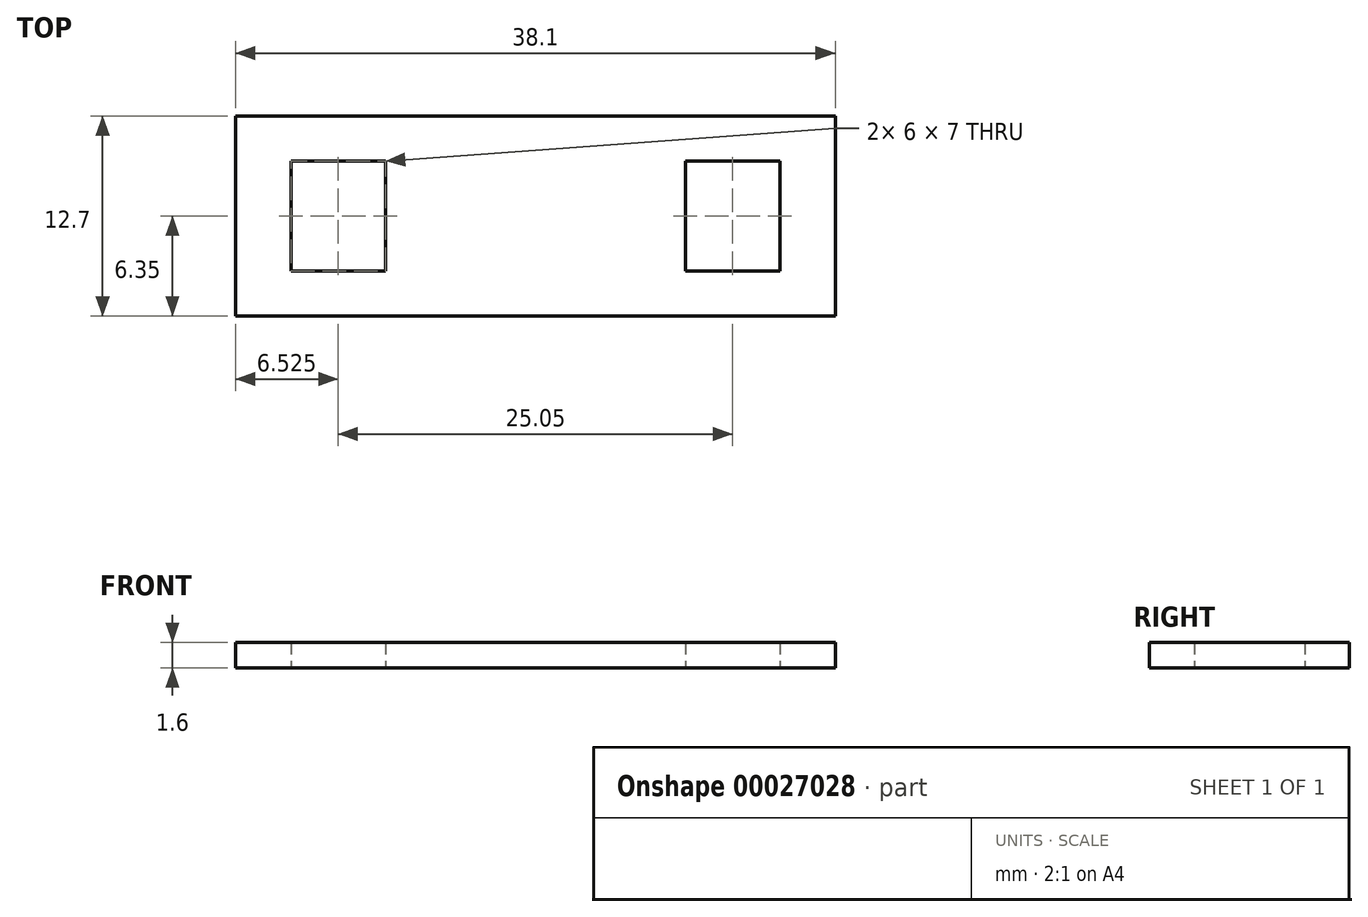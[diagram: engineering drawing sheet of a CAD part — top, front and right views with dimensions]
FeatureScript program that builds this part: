
annotation { "Feature Type Name" : "Feature", "Feature Type Description" : "" }
export const myFeature = defineFeature(function(context is Context, id is Id, definition is map)
    precondition{}
    {
        {
            var Q0;
            Q0=qCreatedBy(makeId("Top.planeOp"),FACE);
            var sketch = newSketch(context, id + "F0", { "sketchPlane" : qUnion([Q0])});
            skLineSegment(sketch, "E0.rect.bottom", {"start": v(19.05, -6.35) * mm, "end": v(-19.05, -6.35) * mm});
            skLineSegment(sketch, "E0.rect.top", {"start": v(19.05, 6.35) * mm, "end": v(-19.05, 6.35) * mm});
            skLineSegment(sketch, "E0.rect.left", {"start": v(19.05, -6.35) * mm, "end": v(19.05, 6.35) * mm});
            skLineSegment(sketch, "E0.rect.right", {"start": v(-19.05, -6.35) * mm, "end": v(-19.05, 6.35) * mm});
            skPoint(sketch, "E0.rect.middle", {"position": v(0, 0) * mm});
            skLineSegment(sketch, "E1.rect.bottom", {"start": v(9.53, 3.5) * mm, "end": v(15.53, 3.5) * mm});
            skLineSegment(sketch, "E1.rect.top", {"start": v(9.53, -3.5) * mm, "end": v(15.53, -3.5) * mm});
            skLineSegment(sketch, "E1.rect.left", {"start": v(9.53, 3.5) * mm, "end": v(9.53, -3.5) * mm});
            skLineSegment(sketch, "E1.rect.right", {"start": v(15.53, 3.5) * mm, "end": v(15.52, -3.5) * mm});
            skPoint(sketch, "E1.rect.middle", {"position": v(12.53, 0) * mm});
            skLineSegment(sketch, "E2.rect.bottom", {"start": v(-15.53, 3.5) * mm, "end": v(-9.53, 3.5) * mm});
            skLineSegment(sketch, "E2.rect.top", {"start": v(-15.53, -3.5) * mm, "end": v(-9.52, -3.5) * mm});
            skLineSegment(sketch, "E2.rect.left", {"start": v(-15.52, 3.5) * mm, "end": v(-15.53, -3.5) * mm});
            skLineSegment(sketch, "E2.rect.right", {"start": v(-9.53, 3.5) * mm, "end": v(-9.53, -3.5) * mm});
            skPoint(sketch, "E2.rect.middle", {"position": v(-12.53, 0) * mm});
            skLineSegment(sketch, "E3", {"start": v(0, 0) * mm, "end": v(9.53, 0) * mm, "construction": true});
            skLineSegment(sketch, "E4", {"start": v(0, 0) * mm, "end": v(-9.53, 0) * mm, "construction": true});
            skSolve(sketch);
        }
        {
            var Q0;
            Q0=makeQuery(id+"F0.imprint","IMPRINT",FACE,{"disambiguationData":[TD([[makeQuery(id+"F0.imprint","IMPRINT",EDGE,{"derivedFrom":sQuery(id+"F0.wireOp",EDGE,"E0.rect.bottom")}),-1.0]])]});
            extrude(context, id + "F1", {"entities" : qUnion([Q0]), "depth" : 1.6 * mm});
        }
    });
